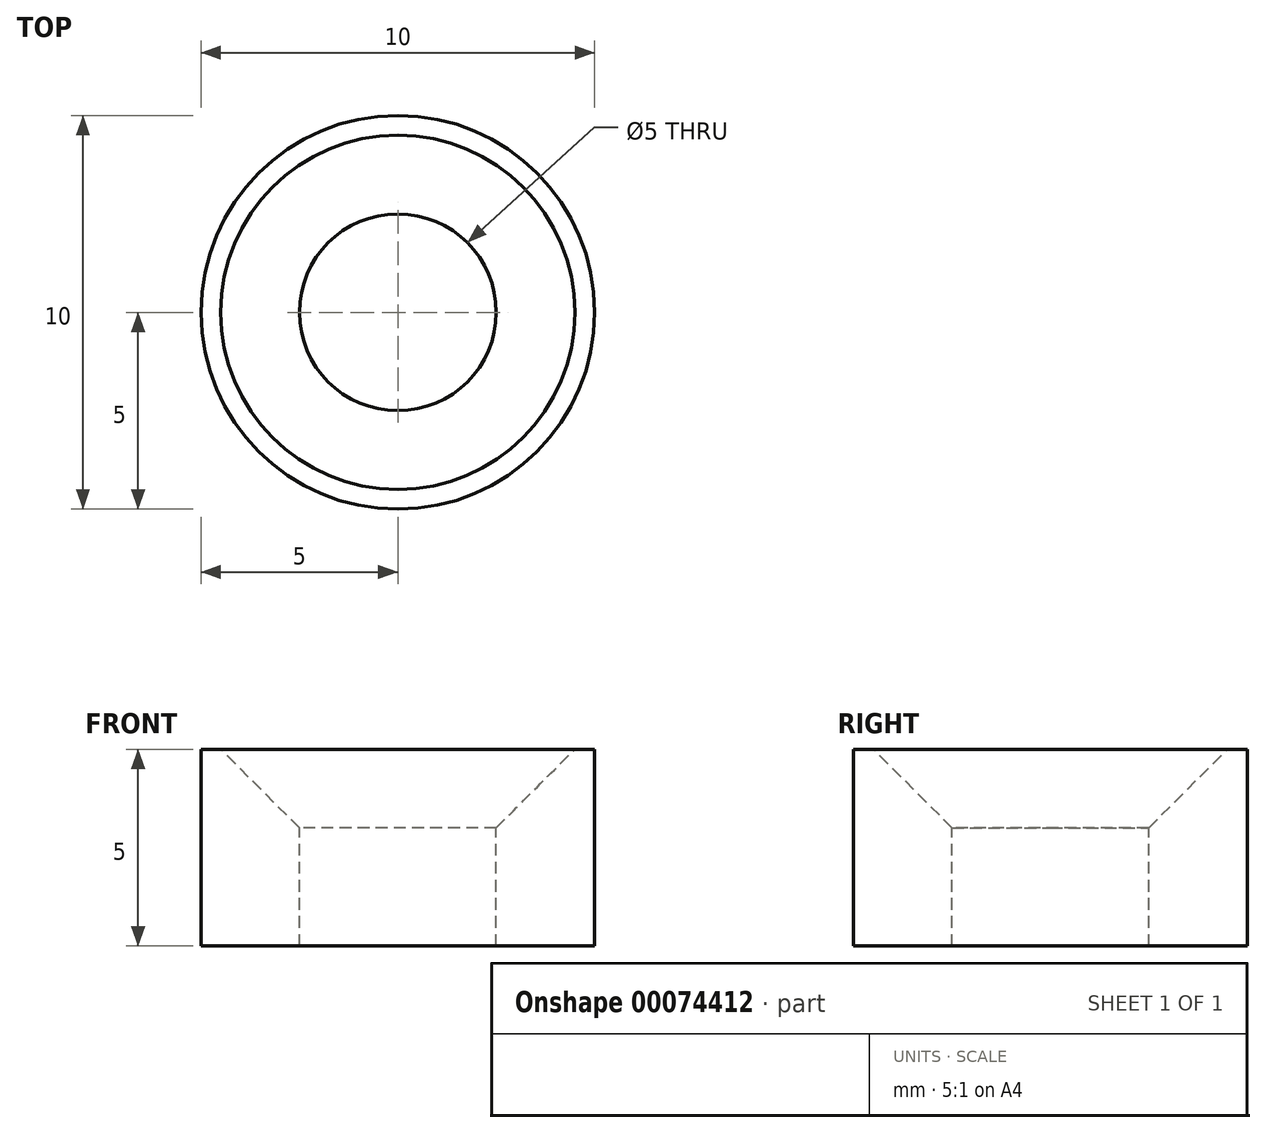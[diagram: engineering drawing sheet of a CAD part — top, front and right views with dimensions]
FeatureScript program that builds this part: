
annotation { "Feature Type Name" : "Feature", "Feature Type Description" : "" }
export const myFeature = defineFeature(function(context is Context, id is Id, definition is map)
    precondition{}
    {
        {
            var Q0;
            Q0=qCreatedBy(makeId("Front.planeOp"),FACE);
            var sketch = newSketch(context, id + "F0", { "sketchPlane" : qUnion([Q0])});
            skLineSegment(sketch, "E0", {"start": v(0, 0) * mm, "end": v(2.5, 0) * mm, "construction": true});
            skLineSegment(sketch, "E1", {"start": v(2.5, 0) * mm, "end": v(5, 0) * mm});
            skLineSegment(sketch, "E2", {"start": v(5, 0) * mm, "end": v(5, 5) * mm});
            skLineSegment(sketch, "E3", {"start": v(5, 5) * mm, "end": v(4.5, 5) * mm});
            skLineSegment(sketch, "E4", {"start": v(4.5, 5) * mm, "end": v(2.5, 3) * mm});
            skLineSegment(sketch, "E5", {"start": v(2.5, 3) * mm, "end": v(2.5, 0) * mm});
            skLineSegment(sketch, "E6", {"start": v(4.5, 5) * mm, "end": v(0, 5) * mm, "construction": true});
            skLineSegment(sketch, "E7", {"start": v(0, 5) * mm, "end": v(0, 0) * mm, "construction": true});
            skSolve(sketch);
        }
        {
            var Q0;
            Q0=makeQuery(id+"F0.imprint","IMPRINT",FACE,{"disambiguationData":[TD([[makeQuery(id+"F0.imprint","IMPRINT",EDGE,{"derivedFrom":sQuery(id+"F0.wireOp",EDGE,"E1")}),1.0]])]});
            var Q1;
            Q1=sQuery(id+"F0.wireOp",EDGE,"E7");
            revolve(context, id + "F1", {"entities" : qUnion([Q0]), "axis" : qUnion([Q1]), "revolveType" : RevolveType.FULL});
        }
    });
